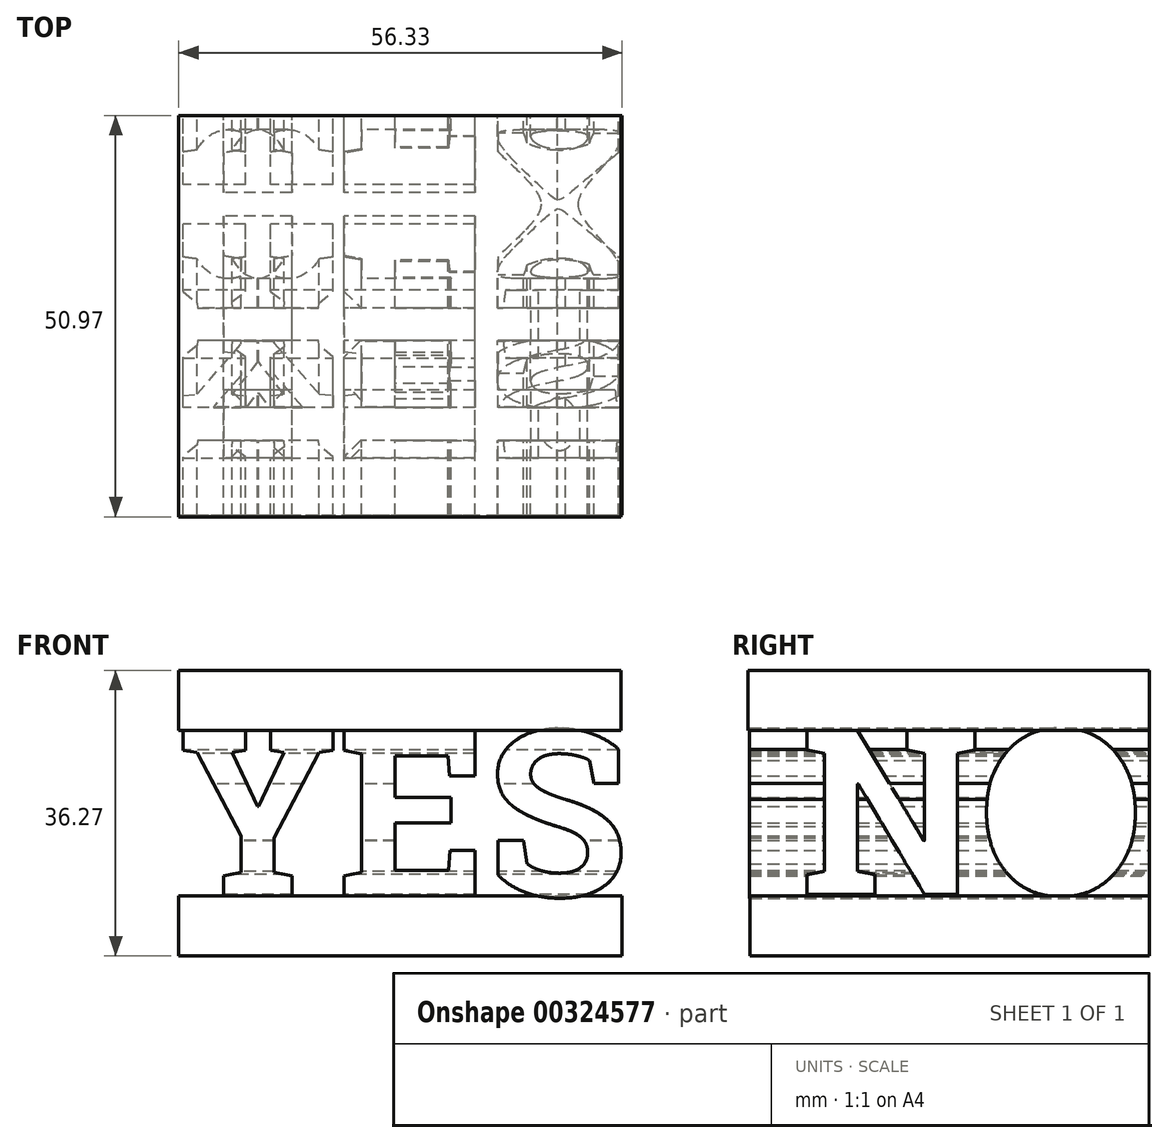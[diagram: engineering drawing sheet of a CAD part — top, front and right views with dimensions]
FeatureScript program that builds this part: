
annotation { "Feature Type Name" : "Feature", "Feature Type Description" : "" }
export const myFeature = defineFeature(function(context is Context, id is Id, definition is map)
    precondition{}
    {
        {
            var Q0;
            Q0=qCreatedBy(makeId("Front.planeOp"),FACE);
            var sketch = newSketch(context, id + "F0", { "sketchPlane" : qUnion([Q0])});
            skText(sketch, "E0", { "text": "YES\n", "fontName": "RobotoSlab-Bold.ttf"});
            const initialGuessF0  = {"E0": [0, -0.0213, 1, 0, 0.0213]};
            skSetInitialGuess(sketch, initialGuessF0);
            skSolve(sketch);
        }
        {
            var Q0;
            Q0 = qSketchRegion(id + "F0", true);
            extrude(context, id + "F1", {"entities" : qUnion([Q0]), "depth" : 50.8 * mm});
        }
        {
            var Q0;
            Q0=qCreatedBy(makeId("Right.planeOp"),FACE);
            var sketch = newSketch(context, id + "F2", { "sketchPlane" : qUnion([Q0])});
            skText(sketch, "E1", { "text": "NO\n", "fontName": "RobotoSlab-Bold.ttf"});
            const initialGuessF2  = {"E1": [-0.04428, -0.0211, 1, 0, 0.0211]};
            skSetInitialGuess(sketch, initialGuessF2);
            skSolve(sketch);
        }
        {
            var Q0;
            Q0 = qSketchRegion(id + "F2", true);
            var Q1;
            Q1=makeQuery(id+"F2.imprint","IMPRINT",FACE,{"disambiguationData":[TD([[makeQuery(id+"F2.imprint","IMPRINT",EDGE,{"derivedFrom":sQuery(id+"F2.wireOp",EDGE,"E1.sketch_text.stroke-34")}),1.0]])]});
            extrude(context, id + "F3", {"entities" : qUnion([Q0, Q1]), "operationType" : NewBodyOperationType.REMOVE, "depth" : 66.3 * mm});
        }
        {
            var Q0;
            {var subQ1=sQuery(id+"F0.wireOp",EDGE,"E0.sketch_text.stroke-20");Q0=makeQuery(id+"F3.boolean.opBoolean","SPLIT",FACE,{"disambiguationData":[TD([makeQuery(id+"F3.opExtrude","SWEPT_FACE",FACE,{"disambiguationData":[OSD([sQuery(id+"F2.wireOp",EDGE,"E1.sketch_text.stroke-31")])]})])],"derivedFrom":makeQuery(id+"F1.opExtrude","SWEPT_FACE",FACE,{"disambiguationData":[OSD([subQ1])]})});}
            var sketch = newSketch(context, id + "F4", { "sketchPlane" : qUnion([Q0])});
            skLineSegment(sketch, "E2.bottom", {"start": v(0, 0) * mm, "end": v(56.17, 0) * mm});
            skLineSegment(sketch, "E2.top", {"start": v(0, -50.97) * mm, "end": v(56.17, -50.97) * mm});
            skLineSegment(sketch, "E2.left", {"start": v(0, 0) * mm, "end": v(0, -50.97) * mm});
            skLineSegment(sketch, "E2.right", {"start": v(56.17, 0) * mm, "end": v(56.17, -50.97) * mm});
            skSolve(sketch);
        }
        {
            var Q0;
            Q0 = qSketchRegion(id + "F4", true);
            extrude(context, id + "F5", {"entities" : qUnion([Q0]), "depth" : 7.62 * mm});
        }
        {
            var Q0;
            {var subQ1=sQuery(id+"F0.wireOp",EDGE,"E0.sketch_text.stroke-28");Q0=makeQuery(id+"F3.boolean.opBoolean","SPLIT",FACE,{"disambiguationData":[TD([makeQuery(id+"F3.opExtrude","SWEPT_FACE",FACE,{"disambiguationData":[OSD([sQuery(id+"F2.wireOp",EDGE,"E1.sketch_text.stroke-26")])]})])],"derivedFrom":makeQuery(id+"F1.opExtrude","SWEPT_FACE",FACE,{"disambiguationData":[OSD([subQ1])]})});}
            var sketch = newSketch(context, id + "F6", { "sketchPlane" : qUnion([Q0])});
            skLineSegment(sketch, "E3.bottom", {"start": v(0, 0) * mm, "end": v(56.33, 0) * mm});
            skLineSegment(sketch, "E3.top", {"start": v(0, 50.73) * mm, "end": v(56.33, 50.73) * mm});
            skLineSegment(sketch, "E3.left", {"start": v(0, 50.73) * mm, "end": v(0, 0) * mm});
            skLineSegment(sketch, "E3.right", {"start": v(56.33, 50.73) * mm, "end": v(56.33, 0) * mm});
            skSolve(sketch);
        }
        {
            var Q0;
            Q0 = qSketchRegion(id + "F6", true);
            extrude(context, id + "F7", {"entities" : qUnion([Q0]), "depth" : 7.62 * mm});
        }
    });
